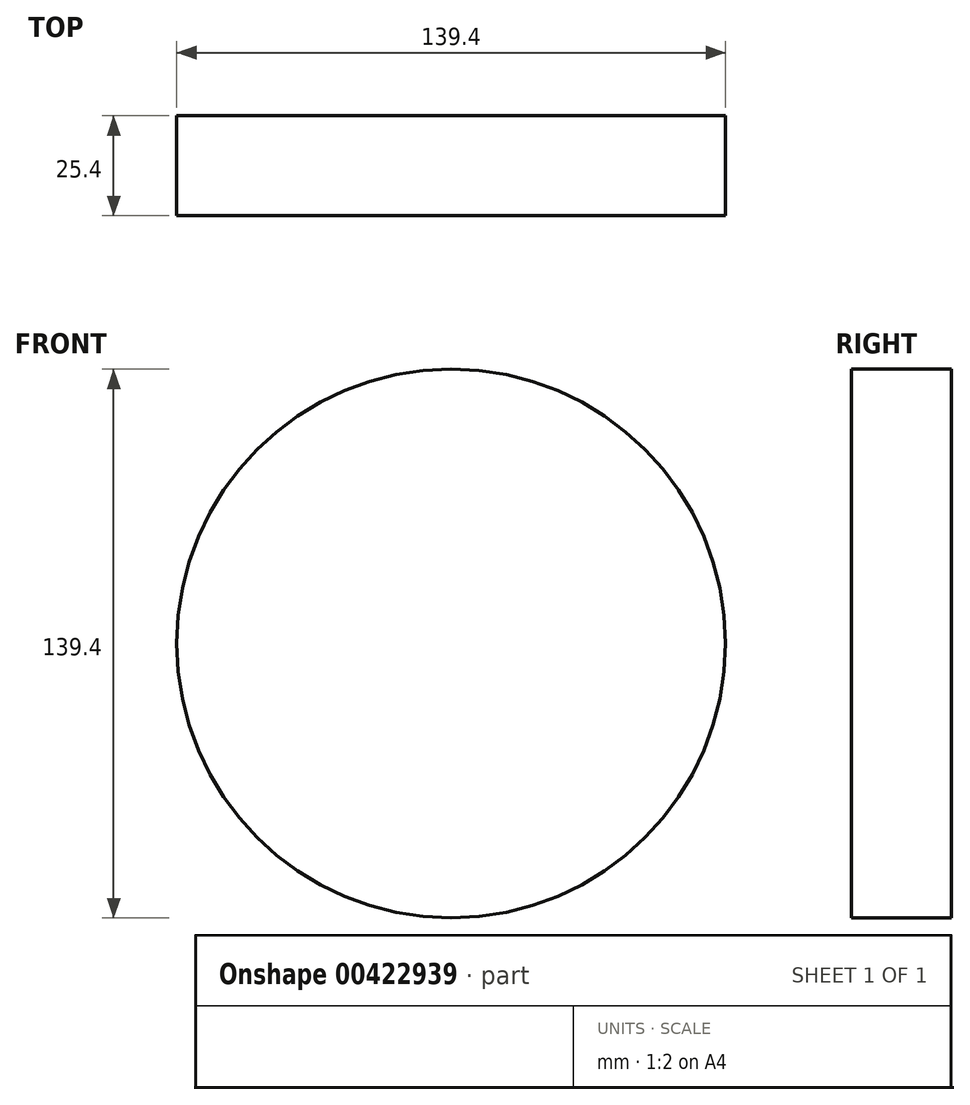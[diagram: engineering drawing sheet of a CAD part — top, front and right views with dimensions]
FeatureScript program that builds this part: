
annotation { "Feature Type Name" : "Feature", "Feature Type Description" : "" }
export const myFeature = defineFeature(function(context is Context, id is Id, definition is map)
    precondition{}
    {
        {
            var Q0;
            Q0=qCreatedBy(makeId("Front.planeOp"),FACE);
            var sketch = newSketch(context, id + "F0", { "sketchPlane" : qUnion([Q0])});
            skCircle(sketch, "E0", {"center": v(0, 0) * mm, "radius": 69.7 * mm});
            skSolve(sketch);
        }
        {
            var Q0;
            Q0=sQuery(id+"F0.wireOp",EDGE,"E0");
            extrude(context, id + "F1", {"bodyType" : ToolBodyType.SURFACE, "surfaceEntities" : qUnion([Q0]), "depth" : 25.4 * mm});
        }
    });
